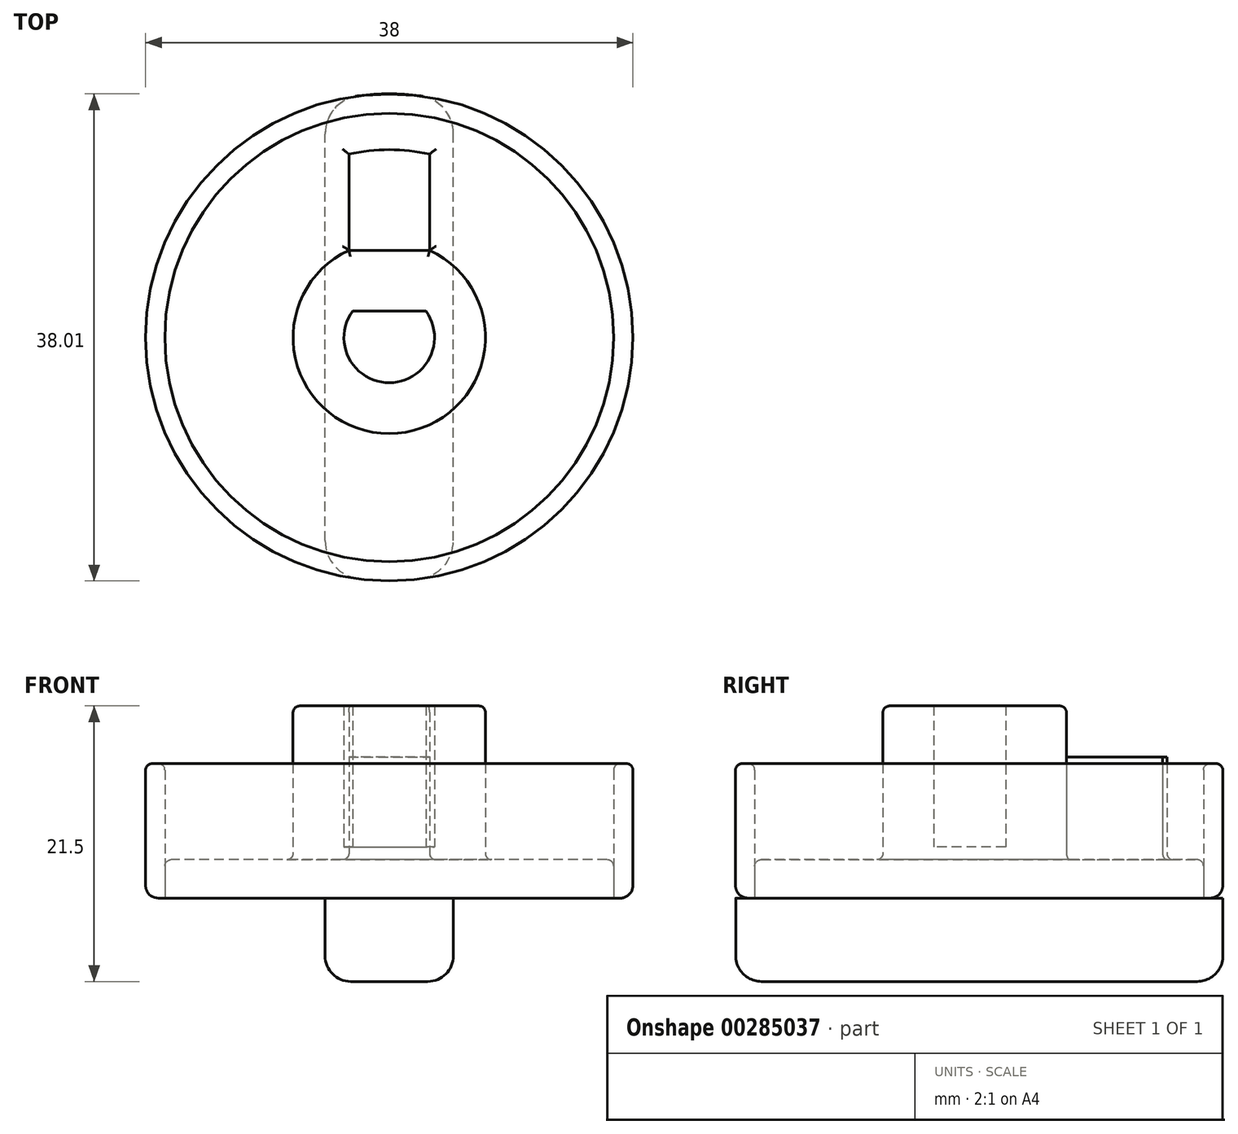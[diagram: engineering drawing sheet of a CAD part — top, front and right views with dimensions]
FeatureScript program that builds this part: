
annotation { "Feature Type Name" : "Feature", "Feature Type Description" : "" }
export const myFeature = defineFeature(function(context is Context, id is Id, definition is map)
    precondition{}
    {
        {
            var Q0;
            Q0=qCreatedBy(makeId("Top.planeOp"),FACE);
            var sketch = newSketch(context, id + "F0", { "sketchPlane" : qUnion([Q0])});
            skCircle(sketch, "E0", {"center": v(0, 0) * mm, "radius": 19 * mm});
            skCircle(sketch, "E1", {"center": v(0, 0) * mm, "radius": 17.5 * mm});
            skArc(sketch, "E2", {"start": v(-3.15, 6.8) * mm, "mid": v(0, -7.5) * mm, "end": v(3.15, 6.8) * mm});
            skArc(sketch, "E3", {"start": v(-2.86, 2.07) * mm, "mid": v(0, -3.53) * mm, "end": v(2.86, 2.07) * mm});
            skLineSegment(sketch, "E4", {"start": v(3.15, 6.8) * mm, "end": v(3.15, 14.3) * mm});
            skArc(sketch, "E5", {"start": v(3.15, 14.3) * mm, "mid": v(0, 14.65) * mm, "end": v(-3.15, 14.3) * mm});
            skLineSegment(sketch, "E6", {"start": v(-3.15, 6.8) * mm, "end": v(-3.15, 14.3) * mm});
            skLineSegment(sketch, "E7", {"start": v(-2.86, 2.07) * mm, "end": v(2.86, 2.07) * mm});
            skLineSegment(sketch, "E8", {"start": v(-3.15, 6.8) * mm, "end": v(3.15, 6.8) * mm});
            skSolve(sketch);
        }
        {
            var Q0;
            Q0=makeQuery(id+"F0.imprint","IMPRINT",FACE,{"disambiguationData":[TD([[makeQuery(id+"F0.imprint","IMPRINT",EDGE,{"derivedFrom":sQuery(id+"F0.wireOp",EDGE,"E2")}),1.0]])]});
            extrude(context, id + "F1", {"entities" : qUnion([Q0]), "depth" : 15 * mm});
        }
        {
            var Q0;
            Q0=makeQuery(id+"F0.imprint","IMPRINT",FACE,{"disambiguationData":[TD([[makeQuery(id+"F0.imprint","IMPRINT",EDGE,{"derivedFrom":sQuery(id+"F0.wireOp",EDGE,"E4")}),1.0]])]});
            extrude(context, id + "F2", {"entities" : qUnion([Q0]), "operationType" : NewBodyOperationType.ADD, "depth" : 11 * mm});
        }
        {
            var Q0;
            Q0=makeQuery(id+"F0.imprint","IMPRINT",FACE,{"disambiguationData":[TD([[makeQuery(id+"F0.imprint","IMPRINT",EDGE,{"derivedFrom":sQuery(id+"F0.wireOp",EDGE,"E1")}),1.0]])]});
            var Q1;
            Q1=makeQuery(id+"F0.imprint","IMPRINT",FACE,{"disambiguationData":[TD([[makeQuery(id+"F0.imprint","IMPRINT",EDGE,{"derivedFrom":sQuery(id+"F0.wireOp",EDGE,"E2")}),1.0]])]});
            var Q2;
            Q2=makeQuery(id+"F0.imprint","IMPRINT",FACE,{"disambiguationData":[TD([[makeQuery(id+"F0.imprint","IMPRINT",EDGE,{"derivedFrom":sQuery(id+"F0.wireOp",EDGE,"E4")}),1.0]])]});
            var Q3;
            Q3=makeQuery(id+"F0.imprint","IMPRINT",FACE,{"disambiguationData":[TD([[makeQuery(id+"F0.imprint","IMPRINT",EDGE,{"derivedFrom":sQuery(id+"F0.wireOp",EDGE,"E3")}),1.0]])]});
            extrude(context, id + "F3", {"entities" : qUnion([Q0, Q1, Q2, Q3]), "operationType" : NewBodyOperationType.ADD, "depth" : 3 * mm});
        }
        {
            var Q0;
            Q0=makeQuery(id+"F0.imprint","IMPRINT",FACE,{"disambiguationData":[TD([[makeQuery(id+"F0.imprint","IMPRINT",EDGE,{"derivedFrom":sQuery(id+"F0.wireOp",EDGE,"E3")}),1.0]])]});
            extrude(context, id + "F4", {"entities" : qUnion([Q0]), "operationType" : NewBodyOperationType.ADD, "depth" : 4 * mm});
        }
        {
            var Q0;
            Q0=makeQuery(id+"F0.imprint","IMPRINT",FACE,{"disambiguationData":[TD([[makeQuery(id+"F0.imprint","IMPRINT",EDGE,{"derivedFrom":sQuery(id+"F0.wireOp",EDGE,"E0")}),1.0]])]});
            extrude(context, id + "F5", {"entities" : qUnion([Q0]), "depth" : 10.5 * mm});
        }
        {
            var Q0;
            Q0=makeQuery(id+"F0.imprint","IMPRINT",FACE,{"disambiguationData":[TD([[makeQuery(id+"F0.imprint","IMPRINT",EDGE,{"derivedFrom":sQuery(id+"F0.wireOp",EDGE,"E1")}),1.0]])]});
            var sketch = newSketch(context, id + "F6", { "sketchPlane" : qUnion([Q0])});
            skLineSegment(sketch, "E9", {"start": v(5, -18.33) * mm, "end": v(5, 18.33) * mm});
            skLineSegment(sketch, "E10.MirrorCS", {"start": v(-5, -18.33) * mm, "end": v(-5, 18.33) * mm});
            skPoint(sketch, "E11.start.orphan", {"position": v(0, 0) * mm});
            skArc(sketch, "E12", {"start": v(-5, -18.33) * mm, "mid": v(0, -18.98) * mm, "end": v(5, -18.33) * mm});
            skArc(sketch, "E13", {"start": v(5, 18.33) * mm, "mid": v(0, 19.01) * mm, "end": v(-5, 18.33) * mm});
            skSolve(sketch);
        }
        {
            var Q0;
            {var subQ0=sQuery(id+"F6.wireOp",EDGE,"E9");var subQ1=makeQuery(id+"F0.imprint","IMPRINT",EDGE,{"derivedFrom":sQuery(id+"F0.wireOp",EDGE,"E1")});var subQ2=makeQuery(id+"F6.imprint","INTERSECT",VERTEX,{"disambiguationData":[OD(0.0)],"derivedFrom":[subQ1,subQ0]});Q0=makeQuery(id+"F6.imprint","IMPRINT",FACE,{"disambiguationData":[TD([[makeQuery(id+"F6.imprint","IMPRINT",EDGE,{"disambiguationData":[TD([[subQ2,-1.0]])],"derivedFrom":subQ0}),1.0]])]});}
            var Q1;
            {var subQ0=makeQuery(id+"F0.imprint","IMPRINT",EDGE,{"derivedFrom":sQuery(id+"F0.wireOp",EDGE,"E4")});Q1=makeQuery(id+"F6.imprint","IMPRINT",FACE,{"disambiguationData":[TD([[makeQuery(id+"F6.imprint","IMPRINT",EDGE,{"derivedFrom":subQ0}),-1.0]])]});}
            var Q2;
            {var subQ4=makeQuery(id+"F0.imprint","IMPRINT",EDGE,{"derivedFrom":sQuery(id+"F0.wireOp",EDGE,"E4")});Q2=makeQuery(id+"F6.imprint","IMPRINT",FACE,{"disambiguationData":[TD([[makeQuery(id+"F6.imprint","IMPRINT",EDGE,{"derivedFrom":subQ4}),1.0]])]});}
            var Q3;
            {var subQ0=sQuery(id+"F6.wireOp",EDGE,"E13");Q3=makeQuery(id+"F6.imprint","IMPRINT",FACE,{"disambiguationData":[TD([[makeQuery(id+"F6.imprint","IMPRINT",EDGE,{"derivedFrom":subQ0}),1.0]])]});}
            var Q4;
            {var subQ0=sQuery(id+"F6.wireOp",EDGE,"E12");Q4=makeQuery(id+"F6.imprint","IMPRINT",FACE,{"disambiguationData":[TD([[makeQuery(id+"F6.imprint","IMPRINT",EDGE,{"derivedFrom":subQ0}),1.0]])]});}
            extrude(context, id + "F7", {"entities" : qUnion([Q0, Q1, Q2, Q3, Q4]), "oppositeDirection" : true, "depth" : 6.5 * mm});
        }
        {
            var Q0;
            Q0=makeQuery(id+"F1.opExtrude","CAP_EDGE",EDGE,{"disambiguationData":[OSD([sQuery(id+"F0.wireOp",EDGE,"E2")])],"isStart":false});
            var Q1;
            Q1=makeQuery(id+"F1.opExtrude","CAP_EDGE",EDGE,{"disambiguationData":[OSD([sQuery(id+"F0.wireOp",EDGE,"E8")])],"isStart":false});
            var Q2;
            Q2=makeQuery(id+"F5.opExtrude","CAP_EDGE",EDGE,{"disambiguationData":[OSD([sQuery(id+"F0.wireOp",EDGE,"E1")])],"isStart":false});
            var Q3;
            Q3=makeQuery(id+"F5.opExtrude","CAP_EDGE",EDGE,{"disambiguationData":[OSD([sQuery(id+"F0.wireOp",EDGE,"E0")])],"isStart":false});
            var Q4;
            Q4=makeQuery(id+"F3.boolean.opBoolean","INTERSECT",EDGE,{"derivedFrom":[makeQuery(id+"F1.opExtrude","SWEPT_FACE",FACE,{"disambiguationData":[OSD([sQuery(id+"F0.wireOp",EDGE,"E2")])]}),makeQuery(id+"F3.opExtrude","CAP_FACE",FACE,{"disambiguationData":[OSD([sQuery(id+"F0.wireOp",EDGE,"E1")])],"isStart":false})]});
            var Q5;
            Q5=makeQuery(id+"F3.boolean.opBoolean","INTERSECT",EDGE,{"derivedFrom":[makeQuery(id+"F2.opExtrude","SWEPT_FACE",FACE,{"disambiguationData":[OSD([sQuery(id+"F0.wireOp",EDGE,"E4")])]}),makeQuery(id+"F3.opExtrude","CAP_FACE",FACE,{"disambiguationData":[OSD([sQuery(id+"F0.wireOp",EDGE,"E1")])],"isStart":false})]});
            var Q6;
            Q6=makeQuery(id+"F3.boolean.opBoolean","INTERSECT",EDGE,{"derivedFrom":[makeQuery(id+"F2.opExtrude","SWEPT_FACE",FACE,{"disambiguationData":[OSD([sQuery(id+"F0.wireOp",EDGE,"E6")])]}),makeQuery(id+"F3.opExtrude","CAP_FACE",FACE,{"disambiguationData":[OSD([sQuery(id+"F0.wireOp",EDGE,"E1")])],"isStart":false})]});
            var Q7;
            Q7=makeQuery(id+"F3.boolean.opBoolean","INTERSECT",EDGE,{"derivedFrom":[makeQuery(id+"F2.opExtrude","SWEPT_FACE",FACE,{"disambiguationData":[OSD([sQuery(id+"F0.wireOp",EDGE,"E5")])]}),makeQuery(id+"F3.opExtrude","CAP_FACE",FACE,{"disambiguationData":[OSD([sQuery(id+"F0.wireOp",EDGE,"E1")])],"isStart":false})]});
            var Q8;
            Q8=makeQuery(id+"F2.opExtrude","CAP_EDGE",EDGE,{"disambiguationData":[OSD([sQuery(id+"F0.wireOp",EDGE,"E8")])],"isStart":false});
            fillet(context, id + "F8", {"entities" : qUnion([Q0, Q1, Q2, Q3, Q4, Q5, Q6, Q7, Q8]), "radius" : .5 * mm, "tangentPropagation" : true, "allowEdgeOverflow" : false});
        }
        {
            var Q0;
            Q0=makeQuery(id+"F3.opExtrude","CAP_EDGE",EDGE,{"disambiguationData":[OSD([sQuery(id+"F0.wireOp",EDGE,"E1")])],"isStart":false});
            fillet(context, id + "F9", {"entities" : qUnion([Q0]), "radius" : .5 * mm, "tangentPropagation" : true, "allowEdgeOverflow" : false});
        }
        {
            var Q0;
            Q0=makeQuery(id+"F5.opExtrude","CAP_EDGE",EDGE,{"disambiguationData":[OSD([sQuery(id+"F0.wireOp",EDGE,"E0")])],"isStart":true});
            fillet(context, id + "F10", {"entities" : qUnion([Q0]), "radius" : 1 * mm, "tangentPropagation" : true, "allowEdgeOverflow" : false});
        }
        {
            var Q0;
            Q0=makeQuery(id+"F7.opExtrude","SWEPT_EDGE",EDGE,{"disambiguationData":[OSD([sQuery(id+"F6.wireOp",EDGE,"E10.MirrorCS"),sQuery(id+"F6.wireOp",EDGE,"E12")])]});
            var Q1;
            Q1=makeQuery(id+"F7.opExtrude","SWEPT_EDGE",EDGE,{"disambiguationData":[OSD([sQuery(id+"F6.wireOp",EDGE,"E10.MirrorCS"),sQuery(id+"F6.wireOp",EDGE,"E13")])]});
            var Q2;
            Q2=makeQuery(id+"F7.opExtrude","SWEPT_EDGE",EDGE,{"disambiguationData":[OSD([sQuery(id+"F6.wireOp",EDGE,"E9"),sQuery(id+"F6.wireOp",EDGE,"E13")])]});
            var Q3;
            Q3=makeQuery(id+"F7.opExtrude","SWEPT_EDGE",EDGE,{"disambiguationData":[OSD([sQuery(id+"F6.wireOp",EDGE,"E9"),sQuery(id+"F6.wireOp",EDGE,"E12")])]});
            fillet(context, id + "F11", {"entities" : qUnion([Q0, Q1, Q2, Q3]), "radius" : 3 * mm, "tangentPropagation" : true, "allowEdgeOverflow" : false});
        }
        {
            var Q0;
            Q0=makeQuery(id+"F7.opExtrude","CAP_FACE",FACE,{"disambiguationData":[OSD([sQuery(id+"F6.wireOp",EDGE,"E9"),sQuery(id+"F6.wireOp",EDGE,"E10.MirrorCS"),sQuery(id+"F6.wireOp",EDGE,"E12"),sQuery(id+"F6.wireOp",EDGE,"E13")])],"isStart":false});
            fillet(context, id + "F12", {"entities" : qUnion([Q0]), "radius" : 2 * mm, "tangentPropagation" : true, "allowEdgeOverflow" : false});
        }
    });
